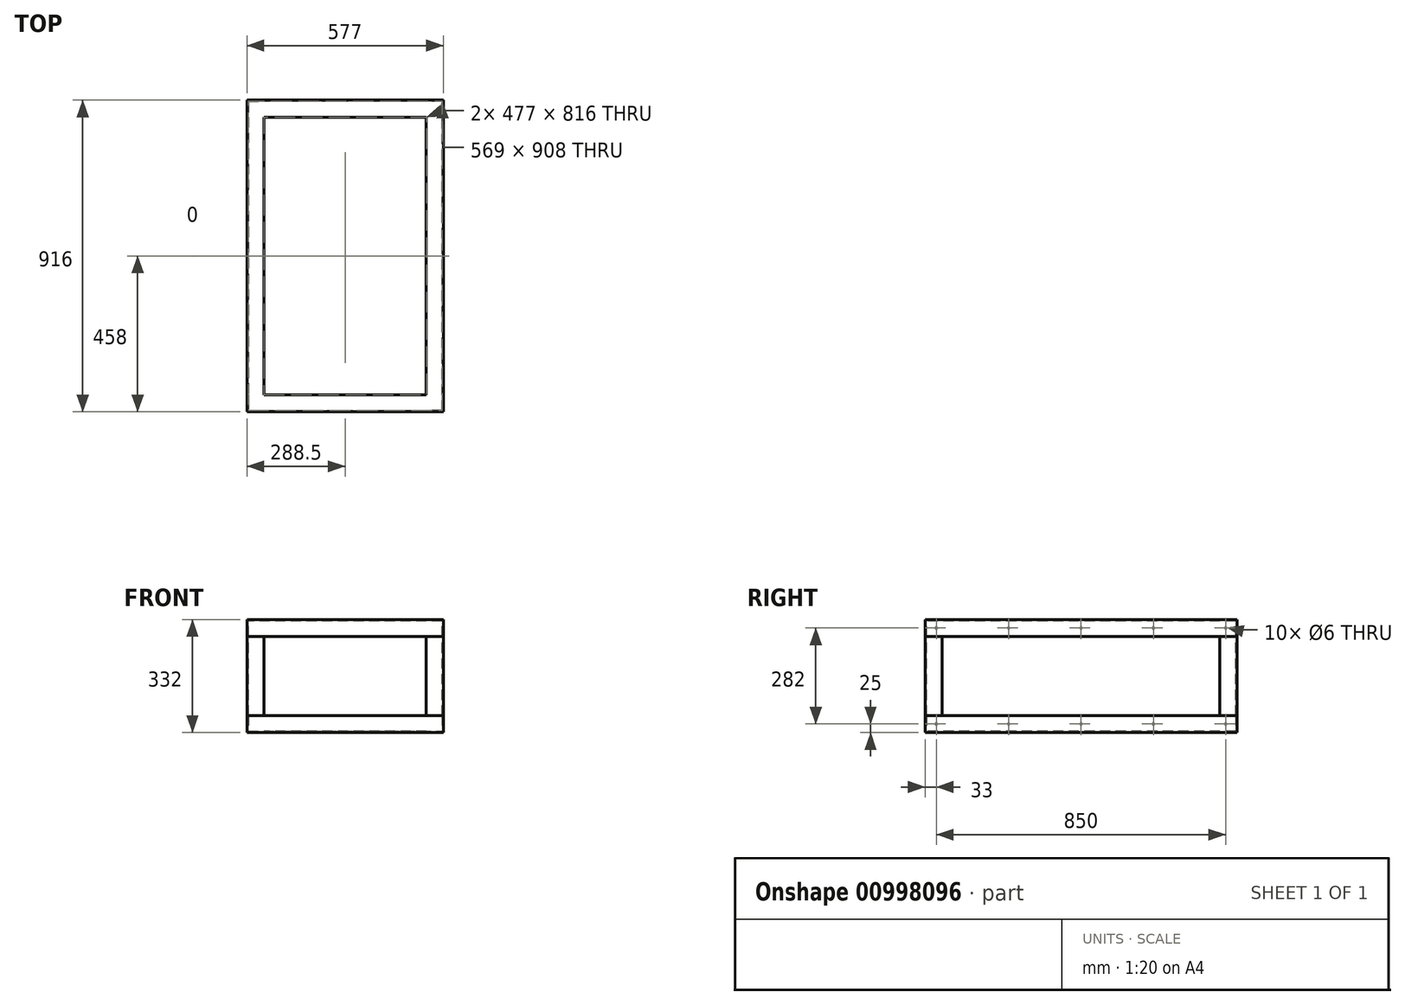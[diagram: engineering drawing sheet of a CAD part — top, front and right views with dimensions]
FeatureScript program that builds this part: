
annotation { "Feature Type Name" : "Feature", "Feature Type Description" : "" }
export const myFeature = defineFeature(function(context is Context, id is Id, definition is map)
    precondition{}
    {
        {
            var Q0;
            Q0=qCreatedBy(makeId("Top.planeOp"),FACE);
            var sketch = newSketch(context, id + "F0", { "sketchPlane" : qUnion([Q0])});
            skLineSegment(sketch, "E0.bottom", {"start": v(0, 0) * mm, "end": v(577, 0) * mm});
            skLineSegment(sketch, "E0.top", {"start": v(0, 916) * mm, "end": v(577, 916) * mm});
            skLineSegment(sketch, "E0.left", {"start": v(0, 0) * mm, "end": v(0, 916) * mm});
            skLineSegment(sketch, "E0.right", {"start": v(577, 0) * mm, "end": v(577, 916) * mm});
            skSolve(sketch);
        }
        {
            var Q0;
            Q0=qCreatedBy(makeId("Right.planeOp"),FACE);
            var sketch = newSketch(context, id + "F1", { "sketchPlane" : qUnion([Q0])});
            skLineSegment(sketch, "E1", {"start": v(0, 50) * mm, "end": v(0, 0) * mm});
            skLineSegment(sketch, "E2", {"start": v(0, 0) * mm, "end": v(50, 0) * mm});
            skLineSegment(sketch, "E3.0", {"start": v(4, 4) * mm, "end": v(50, 4) * mm});
            skLineSegment(sketch, "E3.1", {"start": v(4, 50) * mm, "end": v(4, 4) * mm});
            skLineSegment(sketch, "E4", {"start": v(50, 0) * mm, "end": v(50, 4) * mm});
            skLineSegment(sketch, "E5", {"start": v(0, 50) * mm, "end": v(4, 50) * mm});
            skSolve(sketch);
        }
        {
            var Q0;
            Q0=makeQuery(id+"F1.imprint","IMPRINT",FACE,{"disambiguationData":[TD([[makeQuery(id+"F1.imprint","IMPRINT",EDGE,{"derivedFrom":sQuery(id+"F1.wireOp",EDGE,"E1")}),1.0]])]});
            var Q1;
            Q1=sQuery(id+"F0.wireOp",EDGE,"E0.bottom");
            var Q2;
            Q2=sQuery(id+"F0.wireOp",EDGE,"E0.right");
            var Q3;
            Q3=sQuery(id+"F0.wireOp",EDGE,"E0.top");
            var Q4;
            Q4=sQuery(id+"F0.wireOp",EDGE,"E0.left");
            sweep(context, id + "F2", {"profiles" : qUnion([Q0]), "path" : qUnion([Q1, Q2, Q3, Q4])});
        }
        {
            var Q0;
            Q0=qCreatedBy(makeId("Top.planeOp"),FACE);
            cPlane(context, id + "F3", {"entities" : qUnion([Q0]), "cplaneType" : CPlaneType.OFFSET, "offset" : (332 / 2) * mm, "width" : 150 * mm, "height" : 150 * mm});
        }
        {
            var Q0;
            Q0=makeQuery(id+"F2.opSweep","SWEPT_BODY",BODY,{"disambiguationData":[OSD([sQuery(id+"F0.wireOp",EDGE,"E0.left"),sQuery(id+"F1.wireOp",EDGE,"E1"),sQuery(id+"F1.wireOp",EDGE,"E2"),sQuery(id+"F1.wireOp",EDGE,"E3.0"),sQuery(id+"F1.wireOp",EDGE,"E3.1"),sQuery(id+"F1.wireOp",EDGE,"E4"),sQuery(id+"F1.wireOp",EDGE,"E5")])]});
            var Q1;
            Q1=qCreatedBy(id+"F3.planeOp",FACE);
            mirror(context, id + "F4", {"entities" : qUnion([Q0]), "mirrorPlane" : qUnion([Q1])});
        }
        {
            var Q0;
            Q0=makeQuery(id+"F2.opSweep","SWEPT_FACE",FACE,{"disambiguationData":[OSD([sQuery(id+"F0.wireOp",EDGE,"E0.bottom"),sQuery(id+"F1.wireOp",EDGE,"E1")])]});
            var sketch = newSketch(context, id + "F5", { "sketchPlane" : qUnion([Q0])});
            skLineSegment(sketch, "E6", {"start": v(0, 50) * mm, "end": v(0, 282) * mm});
            skSolve(sketch);
        }
        {
            var Q0;
            Q0=makeQuery(id+"F2.opSweep","SWEPT_FACE",FACE,{"disambiguationData":[OSD([sQuery(id+"F0.wireOp",EDGE,"E0.bottom"),sQuery(id+"F1.wireOp",EDGE,"E5")])]});
            var sketch = newSketch(context, id + "F6", { "sketchPlane" : qUnion([Q0])});
            skLineSegment(sketch, "E7", {"start": v(0, 50) * mm, "end": v(0, 0) * mm});
            skLineSegment(sketch, "E8", {"start": v(0, 0) * mm, "end": v(50, 0) * mm});
            skLineSegment(sketch, "E9.0", {"start": v(5, 5) * mm, "end": v(50, 5) * mm});
            skLineSegment(sketch, "E9.1", {"start": v(5, 50) * mm, "end": v(5, 5) * mm});
            skLineSegment(sketch, "E10", {"start": v(0, 50) * mm, "end": v(5, 50) * mm});
            skLineSegment(sketch, "E11", {"start": v(50, 5) * mm, "end": v(50, 0) * mm});
            skSolve(sketch);
        }
        {
            var Q0;
            Q0=makeQuery(id+"F6.imprint","IMPRINT",FACE,{"disambiguationData":[TD([[makeQuery(id+"F6.imprint","IMPRINT",EDGE,{"derivedFrom":sQuery(id+"F6.wireOp",EDGE,"E7")}),1.0]])]});
            var Q1;
            Q1=sQuery(id+"F5.wireOp",EDGE,"E6");
            sweep(context, id + "F7", {"profiles" : qUnion([Q0]), "path" : qUnion([Q1])});
        }
        {
            var Q0;
            Q0=makeQuery(id+"F2.opSweep","SWEPT_EDGE",EDGE,{"disambiguationData":[OSD([sQuery(id+"F0.wireOp",EDGE,"E0.left"),sQuery(id+"F1.wireOp",EDGE,"E1"),sQuery(id+"F1.wireOp",EDGE,"E2")])]});
            cPoint(context, id + "F8", {"entities" : qUnion([Q0]), "parameter" : 0.5});
        }
        {
            var Q0;
            Q0=qCreatedBy(id+"F8",VERTEX);
            var Q1;
            Q1=makeQuery(id+"F2.opSweep","SWEPT_EDGE",EDGE,{"disambiguationData":[OSD([sQuery(id+"F0.wireOp",EDGE,"E0.left"),sQuery(id+"F1.wireOp",EDGE,"E1"),sQuery(id+"F1.wireOp",EDGE,"E2")])]});
            cPlane(context, id + "F9", {"entities" : qUnion([Q0, Q1]), "cplaneType" : CPlaneType.LINE_POINT, "offset" : 531 * mm, "oppositeDirection" : true, "width" : 150 * mm, "height" : 150 * mm});
        }
        {
            var Q0;
            Q0=makeQuery(id+"F7.opSweep","SWEPT_BODY",BODY,{"disambiguationData":[OSD([sQuery(id+"F5.wireOp",EDGE,"E6"),sQuery(id+"F6.wireOp",EDGE,"E7"),sQuery(id+"F6.wireOp",EDGE,"E8"),sQuery(id+"F6.wireOp",EDGE,"E9.0"),sQuery(id+"F6.wireOp",EDGE,"E9.1"),sQuery(id+"F6.wireOp",EDGE,"E10"),sQuery(id+"F6.wireOp",EDGE,"E11")])]});
            var Q1;
            Q1=qCreatedBy(id+"F9.planeOp",FACE);
            mirror(context, id + "F10", {"entities" : qUnion([Q0]), "mirrorPlane" : qUnion([Q1])});
        }
        {
            var Q0;
            Q0=makeQuery(id+"F2.opSweep","SWEPT_EDGE",EDGE,{"disambiguationData":[OSD([sQuery(id+"F0.wireOp",EDGE,"E0.bottom"),sQuery(id+"F1.wireOp",EDGE,"E1"),sQuery(id+"F1.wireOp",EDGE,"E2")])]});
            cPoint(context, id + "F11", {"entities" : qUnion([Q0]), "parameter" : 0.5});
        }
        {
            var Q0;
            Q0=makeQuery(id+"F2.opSweep","SWEPT_EDGE",EDGE,{"disambiguationData":[OSD([sQuery(id+"F0.wireOp",EDGE,"E0.bottom"),sQuery(id+"F1.wireOp",EDGE,"E1"),sQuery(id+"F1.wireOp",EDGE,"E2")])]});
            var Q1;
            Q1=qCreatedBy(id+"F11",VERTEX);
            cPlane(context, id + "F12", {"entities" : qUnion([Q0, Q1]), "cplaneType" : CPlaneType.LINE_POINT, "offset" : 256 * mm, "width" : 150 * mm, "height" : 150 * mm});
        }
        {
            var Q0;
            Q0=makeQuery(id+"F7.opSweep","SWEPT_BODY",BODY,{"disambiguationData":[OSD([sQuery(id+"F5.wireOp",EDGE,"E6"),sQuery(id+"F6.wireOp",EDGE,"E7"),sQuery(id+"F6.wireOp",EDGE,"E8"),sQuery(id+"F6.wireOp",EDGE,"E9.0"),sQuery(id+"F6.wireOp",EDGE,"E9.1"),sQuery(id+"F6.wireOp",EDGE,"E10"),sQuery(id+"F6.wireOp",EDGE,"E11")])]});
            var Q1;
            Q1=makeQuery(id+"F10.opPattern","COPY",BODY,{"derivedFrom":makeQuery(id+"F7.opSweep","SWEPT_BODY",BODY,{"disambiguationData":[OSD([sQuery(id+"F5.wireOp",EDGE,"E6"),sQuery(id+"F6.wireOp",EDGE,"E7"),sQuery(id+"F6.wireOp",EDGE,"E8"),sQuery(id+"F6.wireOp",EDGE,"E9.0"),sQuery(id+"F6.wireOp",EDGE,"E9.1"),sQuery(id+"F6.wireOp",EDGE,"E10"),sQuery(id+"F6.wireOp",EDGE,"E11")])]}),"instanceName":"1"});
            var Q2;
            Q2=qCreatedBy(id+"F12.planeOp",FACE);
            mirror(context, id + "F13", {"entities" : qUnion([Q0, Q1]), "mirrorPlane" : qUnion([Q2])});
        }
        {
            var Q0;
            Q0=makeQuery(id+"F4.opPattern","COPY",FACE,{"derivedFrom":makeQuery(id+"F2.opSweep","SWEPT_FACE",FACE,{"disambiguationData":[OSD([sQuery(id+"F0.wireOp",EDGE,"E0.left"),sQuery(id+"F1.wireOp",EDGE,"E1")])]}),"instanceName":"1"});
            var sketch = newSketch(context, id + "F14", { "sketchPlane" : qUnion([Q0])});
            skCircle(sketch, "E12", {"center": v(-883, 307) * mm, "radius": 3 * mm});
            skPoint(sketch, "E12.centerSnap0", {"position": v(-916, 307) * mm});
            skCircle(sketch, "E13", {"center": v(-670.5, 307) * mm, "radius": 3 * mm});
            skCircle(sketch, "E14", {"center": v(-245.5, 307) * mm, "radius": 3 * mm});
            skCircle(sketch, "E15", {"center": v(-33, 307) * mm, "radius": 3 * mm});
            skCircle(sketch, "E16.MirrorC", {"center": v(-245.5, 25) * mm, "radius": 3 * mm});
            skCircle(sketch, "E17.MirrorC", {"center": v(-670.5, 25) * mm, "radius": 3 * mm});
            skCircle(sketch, "E18.MirrorC", {"center": v(-33, 25) * mm, "radius": 3 * mm});
            skCircle(sketch, "E19.MirrorC", {"center": v(-883, 25) * mm, "radius": 3 * mm});
            skCircle(sketch, "E20", {"center": v(-458, 307) * mm, "radius": 3 * mm});
            skPoint(sketch, "E20.centerSnap0", {"position": v(-458, 282) * mm});
            skCircle(sketch, "E21", {"center": v(-458, 25) * mm, "radius": 3 * mm});
            skSolve(sketch);
        }
        {
            var Q0;
            Q0=qSketchRegion(id+"F14",true);
            var Q1;
            Q1=makeQuery(id+"F4.opPattern","COPY",FACE,{"derivedFrom":makeQuery(id+"F2.opSweep","SWEPT_FACE",FACE,{"disambiguationData":[OSD([sQuery(id+"F0.wireOp",EDGE,"E0.right"),sQuery(id+"F1.wireOp",EDGE,"E1")])]}),"instanceName":"1"});
            extrude(context, id + "F15", {"entities" : qUnion([Q0]), "operationType" : NewBodyOperationType.REMOVE, "endBound" : BoundingType.UP_TO_NEXT, "oppositeDirection" : true, "depth" : 25 * mm, "endBoundEntityFace" : qUnion([Q1]), "offsetDistance" : 25 * mm});
        }
    });
